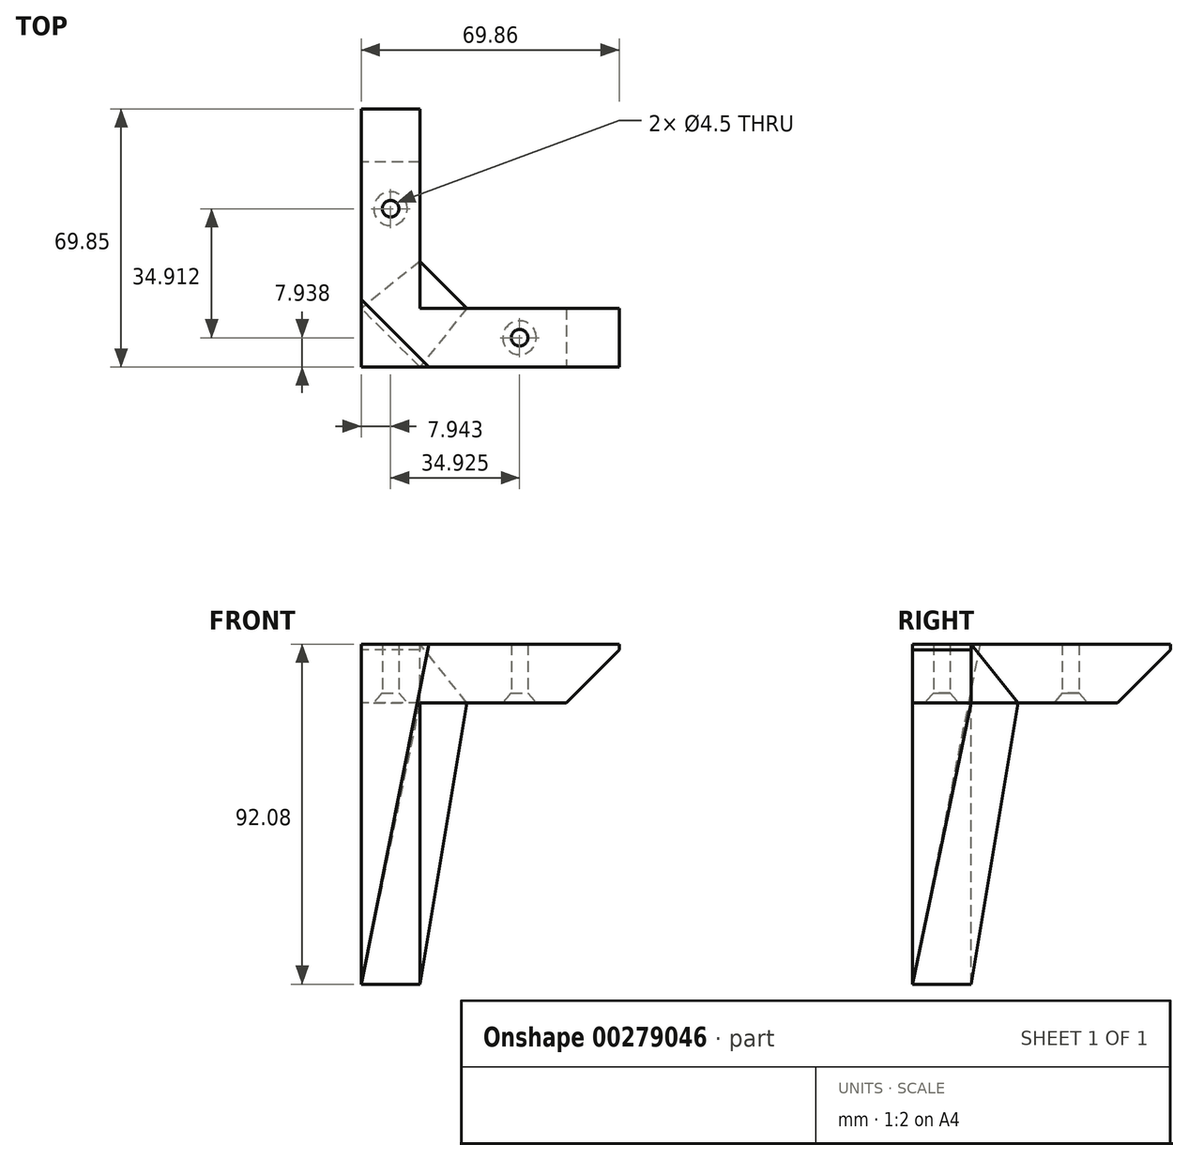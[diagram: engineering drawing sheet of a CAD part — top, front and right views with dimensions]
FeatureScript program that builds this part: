
annotation { "Feature Type Name" : "Feature", "Feature Type Description" : "" }
export const myFeature = defineFeature(function(context is Context, id is Id, definition is map)
    precondition{}
    {
        {
            var Q0;
            Q0=qCreatedBy(makeId("Top.planeOp"),FACE);
            var sketch = newSketch(context, id + "F0", { "sketchPlane" : qUnion([Q0])});
            skLineSegment(sketch, "E0.bottom", {"start": v(0, 0) * mm, "end": v(-15.88, 0) * mm});
            skLineSegment(sketch, "E0.top", {"start": v(0, 69.85) * mm, "end": v(-15.88, 69.85) * mm});
            skLineSegment(sketch, "E0.left", {"start": v(0, 15.87) * mm, "end": v(0, 69.85) * mm});
            skLineSegment(sketch, "E0.right", {"start": v(-15.88, 0) * mm, "end": v(-15.88, 69.85) * mm});
            skLineSegment(sketch, "E1.bottom", {"start": v(0, 0) * mm, "end": v(53.98, 0) * mm});
            skLineSegment(sketch, "E1.top", {"start": v(0, 15.87) * mm, "end": v(53.98, 15.87) * mm});
            skLineSegment(sketch, "E1.right", {"start": v(53.98, 0) * mm, "end": v(53.98, 15.87) * mm});
            skSolve(sketch);
        }
        {
            var Q0;
            Q0=makeQuery(id+"F0.imprint","IMPRINT",FACE,{"disambiguationData":[TD([[makeQuery(id+"F0.imprint","IMPRINT",EDGE,{"derivedFrom":sQuery(id+"F0.wireOp",EDGE,"E0.bottom")}),-1.0]])]});
            extrude(context, id + "F1", {"entities" : qUnion([Q0]), "depth" : 15.88 * mm});
        }
        {
            var Q0;
            Q0=makeQuery(id+"F1.opExtrude","CAP_FACE",FACE,{"disambiguationData":[OSD([sQuery(id+"F0.wireOp",EDGE,"E0.bottom"),sQuery(id+"F0.wireOp",EDGE,"E0.top"),sQuery(id+"F0.wireOp",EDGE,"E0.left"),sQuery(id+"F0.wireOp",EDGE,"E0.right"),sQuery(id+"F0.wireOp",EDGE,"E1.bottom"),sQuery(id+"F0.wireOp",EDGE,"E1.top"),sQuery(id+"F0.wireOp",EDGE,"E1.right")])],"isStart":true});
            var sketch = newSketch(context, id + "F2", { "sketchPlane" : qUnion([Q0])});
            skLineSegment(sketch, "E2.bottom", {"start": v(-15.88, 0) * mm, "end": v(0, 0) * mm});
            skLineSegment(sketch, "E2.top", {"start": v(-15.88, -15.87) * mm, "end": v(0, -15.87) * mm});
            skLineSegment(sketch, "E2.left", {"start": v(-15.88, 0) * mm, "end": v(-15.88, -15.87) * mm});
            skLineSegment(sketch, "E2.right", {"start": v(0, 0) * mm, "end": v(0, -15.87) * mm});
            skSolve(sketch);
        }
        {
            var Q0;
            Q0=makeQuery(id+"F2.imprint","IMPRINT",FACE,{"disambiguationData":[TD([[makeQuery(id+"F2.imprint","IMPRINT",EDGE,{"derivedFrom":sQuery(id+"F2.wireOp",EDGE,"E2.bottom")}),1.0]])]});
            extrude(context, id + "F3", {"entities" : qUnion([Q0]), "operationType" : NewBodyOperationType.ADD, "depth" : 76.2 * mm});
        }
        {
            var Q0;
            Q0=makeQuery(id+"F3.opExtrude","CAP_FACE",FACE,{"disambiguationData":[OSD([sQuery(id+"F2.wireOp",EDGE,"E2.bottom"),sQuery(id+"F2.wireOp",EDGE,"E2.top"),sQuery(id+"F2.wireOp",EDGE,"E2.left"),sQuery(id+"F2.wireOp",EDGE,"E2.right")])],"isStart":false});
            var sketch = newSketch(context, id + "F4", { "sketchPlane" : qUnion([Q0])});
            skLineSegment(sketch, "E3", {"start": v(-21.68, -5.8) * mm, "end": v(-5.62, 10.26) * mm});
            skSolve(sketch);
        }
        {
            var Q0;
            Q0=sQuery(id+"F4.wireOp",EDGE,"E3");
            cPlane(context, id + "F5", {"entities" : qUnion([Q0]), "cplaneType" : CPlaneType.LINE_ANGLE, "offset" : 25.4 * mm, "angle" : 82 * degree, "width" : 152.4 * mm, "height" : 152.4 * mm});
        }
        {
            var Q0;
            Q0=qCreatedBy(id+"F5.planeOp",FACE);
            var sketch = newSketch(context, id + "F6", { "sketchPlane" : qUnion([Q0])});
            skLineSegment(sketch, "E4.bottom", {"start": v(52.37, 33.7) * mm, "end": v(-53.54, 33.7) * mm});
            skLineSegment(sketch, "E4.top", {"start": v(52.37, -104.46) * mm, "end": v(-53.54, -104.46) * mm});
            skLineSegment(sketch, "E4.left", {"start": v(52.37, 33.7) * mm, "end": v(52.37, -104.46) * mm});
            skLineSegment(sketch, "E4.right", {"start": v(-53.54, 33.7) * mm, "end": v(-53.54, -104.46) * mm});
            skSolve(sketch);
        }
        {
            var Q0;
            Q0 = qSketchRegion(id + "F6", true);
            var Q1;
            Q1=makeQuery(id+"F1.opExtrude","CAP_VERTEX",VERTEX,{"disambiguationData":[OSD([sQuery(id+"F0.wireOp",EDGE,"E0.bottom"),sQuery(id+"F0.wireOp",EDGE,"E0.right")])],"isStart":false});
            extrude(context, id + "F7", {"entities" : qUnion([Q0]), "operationType" : NewBodyOperationType.REMOVE, "endBound" : BoundingType.UP_TO_VERTEX, "oppositeDirection" : true, "endBoundEntityVertex" : qUnion([Q1]), "depth" : 25.4 * mm});
        }
        {
            var Q0;
            Q0=makeQuery(id+"F4.imprint","IMPRINT",FACE,{"disambiguationData":[TD([[makeQuery(id+"F4.imprint","IMPRINT",EDGE,{"derivedFrom":makeQuery(id+"F3.opExtrude","CAP_EDGE",EDGE,{"disambiguationData":[OSD([sQuery(id+"F2.wireOp",EDGE,"E2.bottom")])],"isStart":false})}),1.0]])]});
            var sketch = newSketch(context, id + "F8", { "sketchPlane" : qUnion([Q0])});
            skLineSegment(sketch, "E5", {"start": v(8.34, -7.54) * mm, "end": v(-13.82, -29.7) * mm});
            skSolve(sketch);
        }
        {
            var Q0;
            {var subQ0=sQuery(id+"F0.wireOp",EDGE,"E0.right");var subQ1=sQuery(id+"F0.wireOp",EDGE,"E0.left");var subQ2=sQuery(id+"F0.wireOp",EDGE,"E0.top");var subQ3=sQuery(id+"F0.wireOp",EDGE,"E1.top");var subQ4=makeQuery(id+"F1.opExtrude","CAP_FACE",FACE,{"disambiguationData":[OSD([sQuery(id+"F0.wireOp",EDGE,"E0.bottom"),subQ2,subQ1,subQ0,sQuery(id+"F0.wireOp",EDGE,"E1.bottom"),subQ3,sQuery(id+"F0.wireOp",EDGE,"E1.right")])],"isStart":true});Q0=makeQuery(id+"F3.boolean.opBoolean","SPLIT",FACE,{"disambiguationData":[TD([makeQuery(id+"F1.opExtrude","SWEPT_FACE",FACE,{"disambiguationData":[OSD([subQ2])]})])],"derivedFrom":subQ4});}
            var sketch = newSketch(context, id + "F9", { "sketchPlane" : qUnion([Q0])});
            skLineSegment(sketch, "E6", {"start": v(0, -15.87) * mm, "end": v(0, -28.57) * mm});
            skLineSegment(sketch, "E7", {"start": v(0, -28.57) * mm, "end": v(-15.88, -15.87) * mm});
            skLineSegment(sketch, "E8", {"start": v(-15.88, -15.87) * mm, "end": v(0, -15.87) * mm});
            skSolve(sketch);
        }
        {
            var Q1;
            Q1=makeQuery(id+"F9.imprint","IMPRINT",FACE,{"disambiguationData":[TD([[makeQuery(id+"F9.imprint","IMPRINT",EDGE,{"derivedFrom":sQuery(id+"F9.wireOp",EDGE,"E6")}),-1.0]])]});
            var Q2;
            Q2=makeQuery(id+"F3.opExtrude","CAP_VERTEX",VERTEX,{"disambiguationData":[OSD([sQuery(id+"F0.wireOp",EDGE,"E0.right"),sQuery(id+"F2.wireOp",EDGE,"E2.top"),sQuery(id+"F2.wireOp",EDGE,"E2.left")])],"isStart":false});
            loft(context, id + "F10", {"operationType" : NewBodyOperationType.ADD, "sheetProfilesArray" : [{ "sheetProfileEntities" : qUnion([Q1]) }, { "sheetProfileEntities" : qUnion([Q2]) }]});
        }
        {
            var Q0;
            {var subQ0=sQuery(id+"F0.wireOp",EDGE,"E1.top");var subQ1=sQuery(id+"F0.wireOp",EDGE,"E0.left");var subQ2=sQuery(id+"F0.wireOp",EDGE,"E1.bottom");var subQ3=sQuery(id+"F0.wireOp",EDGE,"E0.bottom");var subQ4=sQuery(id+"F0.wireOp",EDGE,"E1.right");var subQ5=makeQuery(id+"F1.opExtrude","CAP_FACE",FACE,{"disambiguationData":[OSD([subQ3,sQuery(id+"F0.wireOp",EDGE,"E0.top"),subQ1,sQuery(id+"F0.wireOp",EDGE,"E0.right"),subQ2,subQ0,subQ4])],"isStart":true});Q0=makeQuery(id+"F3.boolean.opBoolean","SPLIT",FACE,{"disambiguationData":[TD([makeQuery(id+"F1.opExtrude","SWEPT_FACE",FACE,{"disambiguationData":[OSD([subQ4])]})])],"derivedFrom":subQ5});}
            var sketch = newSketch(context, id + "F11", { "sketchPlane" : qUnion([Q0])});
            skLineSegment(sketch, "E9", {"start": v(0, -15.87) * mm, "end": v(12.7, -15.87) * mm});
            skLineSegment(sketch, "E10", {"start": v(12.7, -15.87) * mm, "end": v(0, 0) * mm});
            skLineSegment(sketch, "E11", {"start": v(0, 0) * mm, "end": v(0, -15.87) * mm});
            skSolve(sketch);
        }
        {
            var Q1;
            Q1=makeQuery(id+"F11.imprint","IMPRINT",FACE,{"disambiguationData":[TD([[makeQuery(id+"F11.imprint","IMPRINT",EDGE,{"derivedFrom":sQuery(id+"F11.wireOp",EDGE,"E9")}),1.0]])]});
            var Q2;
            Q2=makeQuery(id+"F3.opExtrude","CAP_VERTEX",VERTEX,{"disambiguationData":[OSD([sQuery(id+"F0.wireOp",EDGE,"E0.bottom"),sQuery(id+"F0.wireOp",EDGE,"E1.bottom"),sQuery(id+"F2.wireOp",EDGE,"E2.bottom"),sQuery(id+"F2.wireOp",EDGE,"E2.right")])],"isStart":false});
            loft(context, id + "F12", {"operationType" : NewBodyOperationType.ADD, "sheetProfilesArray" : [{ "sheetProfileEntities" : qUnion([Q1]) }, { "sheetProfileEntities" : qUnion([Q2]) }]});
        }
        {
            var Q0;
            {var subQ0=sQuery(id+"F0.wireOp",EDGE,"E0.right");var subQ1=sQuery(id+"F0.wireOp",EDGE,"E0.left");var subQ2=sQuery(id+"F0.wireOp",EDGE,"E0.top");var subQ3=sQuery(id+"F0.wireOp",EDGE,"E1.top");var subQ4=makeQuery(id+"F1.opExtrude","CAP_FACE",FACE,{"disambiguationData":[OSD([sQuery(id+"F0.wireOp",EDGE,"E0.bottom"),subQ2,subQ1,subQ0,sQuery(id+"F0.wireOp",EDGE,"E1.bottom"),subQ3,sQuery(id+"F0.wireOp",EDGE,"E1.right")])],"isStart":true});Q0=makeQuery(id+"F3.boolean.opBoolean","SPLIT",FACE,{"disambiguationData":[TD([makeQuery(id+"F1.opExtrude","SWEPT_FACE",FACE,{"disambiguationData":[OSD([subQ2])]})])],"derivedFrom":subQ4});}
            var sketch = newSketch(context, id + "F13", { "sketchPlane" : qUnion([Q0])});
            skLineSegment(sketch, "E12", {"start": v(0, -15.87) * mm, "end": v(0, -28.57) * mm});
            skLineSegment(sketch, "E13", {"start": v(0, -15.87) * mm, "end": v(12.7, -15.87) * mm});
            skLineSegment(sketch, "E14", {"start": v(12.7, -15.87) * mm, "end": v(0, -28.57) * mm});
            skSolve(sketch);
        }
        {
            var Q1;
            Q1=makeQuery(id+"F13.imprint","IMPRINT",FACE,{"disambiguationData":[TD([[makeQuery(id+"F13.imprint","IMPRINT",EDGE,{"derivedFrom":sQuery(id+"F13.wireOp",EDGE,"E12")}),1.0]])]});
            var Q2;
            Q2=makeQuery(id+"F1.opExtrude","CAP_VERTEX",VERTEX,{"disambiguationData":[OSD([sQuery(id+"F0.wireOp",EDGE,"E0.left"),sQuery(id+"F0.wireOp",EDGE,"E1.top")])],"isStart":false});
            loft(context, id + "F14", {"operationType" : NewBodyOperationType.ADD, "sheetProfilesArray" : [{ "sheetProfileEntities" : qUnion([Q1]) }, { "sheetProfileEntities" : qUnion([Q2]) }]});
        }
        {
            var Q0;
            Q0=makeQuery(id+"F4.imprint","IMPRINT",FACE,{"disambiguationData":[TD([[makeQuery(id+"F4.imprint","IMPRINT",EDGE,{"derivedFrom":makeQuery(id+"F3.opExtrude","CAP_EDGE",EDGE,{"disambiguationData":[OSD([sQuery(id+"F2.wireOp",EDGE,"E2.bottom")])],"isStart":false})}),1.0]])]});
            var sketch = newSketch(context, id + "F15", { "sketchPlane" : qUnion([Q0])});
            skLineSegment(sketch, "E15", {"start": v(0, 0) * mm, "end": v(-15.88, -15.88) * mm});
            skLineSegment(sketch, "E16", {"start": v(0, 0) * mm, "end": v(0, -15.87) * mm});
            skLineSegment(sketch, "E17", {"start": v(-15.88, -15.88) * mm, "end": v(0, -15.88) * mm});
            skSolve(sketch);
        }
        {
            var Q1;
            Q1 = qSketchRegion(id + "F15", true);
            var Q2;
            {var subQ0=sQuery(id+"F0.wireOp",EDGE,"E1.top");var subQ1=sQuery(id+"F0.wireOp",EDGE,"E0.left");Q2=makeQuery(id+"F14.boolean.opBoolean","MERGE",VERTEX,{"derivedFrom":[makeQuery(id+"F12.boolean.opBoolean","MERGE",VERTEX,{"derivedFrom":[makeQuery(id+"F10.boolean.opBoolean","MERGE",VERTEX,{"derivedFrom":[makeQuery(id+"F3.boolean.opBoolean","MERGE",VERTEX,{"derivedFrom":[makeQuery(id+"F1.opExtrude","CAP_VERTEX",VERTEX,{"disambiguationData":[OSD([subQ1,subQ0])],"isStart":true}),makeQuery(id+"F3.opExtrude","CAP_VERTEX",VERTEX,{"disambiguationData":[OSD([subQ1,subQ0,sQuery(id+"F2.wireOp",EDGE,"E2.top"),sQuery(id+"F2.wireOp",EDGE,"E2.right")])],"isStart":true})]}),makeQuery(id+"F10.opLoft","MID_CAP_VERTEX",VERTEX,{"disambiguationData":[OSD([sQuery(id+"F9.wireOp",EDGE,"E6"),sQuery(id+"F9.wireOp",EDGE,"E8")])],"capPos":0.0})]}),makeQuery(id+"F12.opLoft","MID_CAP_VERTEX",VERTEX,{"disambiguationData":[OSD([sQuery(id+"F11.wireOp",EDGE,"E9"),sQuery(id+"F11.wireOp",EDGE,"E11")])],"capPos":0.0})]}),makeQuery(id+"F14.opLoft","MID_CAP_VERTEX",VERTEX,{"disambiguationData":[OSD([sQuery(id+"F13.wireOp",EDGE,"E12"),sQuery(id+"F13.wireOp",EDGE,"E13")])],"capPos":0.0})]});}
            loft(context, id + "F16", {"operationType" : NewBodyOperationType.REMOVE, "sheetProfilesArray" : [{ "sheetProfileEntities" : qUnion([Q1]) }, { "sheetProfileEntities" : qUnion([Q2]) }]});
        }
        {
            var Q0;
            Q0=makeQuery(id+"F10.opLoft","SWEPT_EDGE",EDGE,{"disambiguationData":[OSD([sQuery(id+"F0.wireOp",EDGE,"E0.left"),sQuery(id+"F0.wireOp",EDGE,"E0.right"),sQuery(id+"F2.wireOp",EDGE,"E2.top"),sQuery(id+"F2.wireOp",EDGE,"E2.left"),sQuery(id+"F9.wireOp",EDGE,"E6"),sQuery(id+"F9.wireOp",EDGE,"E7")])]});
            var Q1;
            Q1=makeQuery(id+"F12.opLoft","SWEPT_EDGE",EDGE,{"disambiguationData":[OSD([sQuery(id+"F0.wireOp",EDGE,"E0.bottom"),sQuery(id+"F0.wireOp",EDGE,"E1.bottom"),sQuery(id+"F0.wireOp",EDGE,"E1.top"),sQuery(id+"F2.wireOp",EDGE,"E2.bottom"),sQuery(id+"F2.wireOp",EDGE,"E2.right"),sQuery(id+"F11.wireOp",EDGE,"E9"),sQuery(id+"F11.wireOp",EDGE,"E10")])]});
            cPlane(context, id + "F17", {"entities" : qUnion([Q0, Q1]), "cplaneType" : CPlaneType.LINE_ANGLE, "offset" : 25.4 * mm, "angle" : 0 * degree, "width" : 152.4 * mm, "height" : 152.4 * mm});
        }
        {
            var Q1;
            Q1=makeQuery(id+"F14.opLoft","CAP_FACE",FACE,{"disambiguationData":[OSD([makeQuery(id+"F13.imprint","IMPRINT",FACE,{"disambiguationData":[TD([[makeQuery(id+"F13.imprint","IMPRINT",EDGE,{"derivedFrom":sQuery(id+"F13.wireOp",EDGE,"E12")}),1.0]])]})])],"isStart":true});
            var Q2;
            Q2=makeQuery(id+"F3.opExtrude","CAP_FACE",FACE,{"disambiguationData":[OSD([sQuery(id+"F2.wireOp",EDGE,"E2.bottom"),sQuery(id+"F2.wireOp",EDGE,"E2.top"),sQuery(id+"F2.wireOp",EDGE,"E2.left"),sQuery(id+"F2.wireOp",EDGE,"E2.right")])],"isStart":false});
            loft(context, id + "F18", {"operationType" : NewBodyOperationType.ADD, "sheetProfilesArray" : [{ "sheetProfileEntities" : qUnion([Q1]) }, { "sheetProfileEntities" : qUnion([Q2]) }]});
        }
        {
            var Q0;
            Q0=makeQuery(id+"F3.boolean.opBoolean","MERGE",FACE,{"derivedFrom":[makeQuery(id+"F1.opExtrude","SWEPT_FACE",FACE,{"disambiguationData":[OSD([sQuery(id+"F0.wireOp",EDGE,"E0.right")])]}),makeQuery(id+"F3.opExtrude","SWEPT_FACE",FACE,{"disambiguationData":[OSD([sQuery(id+"F2.wireOp",EDGE,"E2.left")])]})]});
            var sketch = newSketch(context, id + "F19", { "sketchPlane" : qUnion([Q0])});
            skLineSegment(sketch, "E18", {"start": v(-69.85, 0) * mm, "end": v(-69.85, 14.29) * mm});
            skLineSegment(sketch, "E19", {"start": v(-69.85, 14.29) * mm, "end": v(-55.55, 0) * mm});
            skLineSegment(sketch, "E20", {"start": v(-69.85, 0) * mm, "end": v(-55.55, 0) * mm});
            skSolve(sketch);
        }
        {
            var Q0;
            Q0=makeQuery(id+"F19.imprint","IMPRINT",FACE,{"disambiguationData":[TD([[makeQuery(id+"F19.imprint","IMPRINT",EDGE,{"derivedFrom":sQuery(id+"F19.wireOp",EDGE,"E18")}),1.0]])]});
            extrude(context, id + "F20", {"entities" : qUnion([Q0]), "operationType" : NewBodyOperationType.REMOVE, "endBound" : BoundingType.UP_TO_NEXT, "oppositeDirection" : true, "depth" : 25.4 * mm});
        }
        {
            var Q0;
            Q0=makeQuery(id+"F3.boolean.opBoolean","MERGE",FACE,{"derivedFrom":[makeQuery(id+"F1.opExtrude","SWEPT_FACE",FACE,{"disambiguationData":[OSD([sQuery(id+"F0.wireOp",EDGE,"E0.bottom"),sQuery(id+"F0.wireOp",EDGE,"E1.bottom")])]}),makeQuery(id+"F3.opExtrude","SWEPT_FACE",FACE,{"disambiguationData":[OSD([sQuery(id+"F2.wireOp",EDGE,"E2.bottom")])]})]});
            var sketch = newSketch(context, id + "F21", { "sketchPlane" : qUnion([Q0])});
            skLineSegment(sketch, "E21", {"start": v(53.98, 0) * mm, "end": v(53.98, 14.29) * mm});
            skLineSegment(sketch, "E22", {"start": v(53.98, 0) * mm, "end": v(39.69, 0) * mm});
            skLineSegment(sketch, "E23", {"start": v(39.69, 0) * mm, "end": v(53.98, 14.29) * mm});
            skSolve(sketch);
        }
        {
            var Q0;
            Q0=makeQuery(id+"F21.imprint","IMPRINT",FACE,{"disambiguationData":[TD([[makeQuery(id+"F21.imprint","IMPRINT",EDGE,{"derivedFrom":sQuery(id+"F21.wireOp",EDGE,"E21")}),-1.0]])]});
            extrude(context, id + "F22", {"entities" : qUnion([Q0]), "operationType" : NewBodyOperationType.REMOVE, "endBound" : BoundingType.UP_TO_NEXT, "oppositeDirection" : true, "depth" : 25.4 * mm});
        }
        {
            var Q0;
            {var subQ0=sQuery(id+"F0.wireOp",EDGE,"E0.right");var subQ1=sQuery(id+"F0.wireOp",EDGE,"E0.left");var subQ2=sQuery(id+"F0.wireOp",EDGE,"E0.top");var subQ3=sQuery(id+"F0.wireOp",EDGE,"E1.top");var subQ4=makeQuery(id+"F1.opExtrude","CAP_FACE",FACE,{"disambiguationData":[OSD([sQuery(id+"F0.wireOp",EDGE,"E0.bottom"),subQ2,subQ1,subQ0,sQuery(id+"F0.wireOp",EDGE,"E1.bottom"),subQ3,sQuery(id+"F0.wireOp",EDGE,"E1.right")])],"isStart":true});Q0=makeQuery(id+"F3.boolean.opBoolean","SPLIT",FACE,{"disambiguationData":[TD([makeQuery(id+"F1.opExtrude","SWEPT_FACE",FACE,{"disambiguationData":[OSD([subQ2])]})])],"derivedFrom":subQ4});}
            var sketch = newSketch(context, id + "F23", { "sketchPlane" : qUnion([Q0])});
            skLineSegment(sketch, "E24", {"start": v(-15.88, -42.85) * mm, "end": v(0, -42.85) * mm, "construction": true});
            skCircle(sketch, "E25", {"center": v(-7.94, -42.85) * mm, "radius": 4.14 * mm, "construction": true});
            skLineSegment(sketch, "E26", {"start": v(26.99, -15.87) * mm, "end": v(26.99, 0) * mm, "construction": true});
            skCircle(sketch, "E27", {"center": v(26.99, -7.94) * mm, "radius": 3.1 * mm, "construction": true});
            skSolve(sketch);
        }
        {
            var Q0;
            Q0=sQuery(id+"F23.wireOp",VERTEX,"E25.center");
            var Q1;
            Q1=sQuery(id+"F23.wireOp",VERTEX,"E27.center");
            var Q2;
            Q2=makeQuery(id+"F1.opExtrude","SWEPT_BODY",BODY,{"disambiguationData":[OSD([sQuery(id+"F0.wireOp",EDGE,"E0.bottom"),sQuery(id+"F0.wireOp",EDGE,"E0.top"),sQuery(id+"F0.wireOp",EDGE,"E0.left"),sQuery(id+"F0.wireOp",EDGE,"E0.right"),sQuery(id+"F0.wireOp",EDGE,"E1.bottom"),sQuery(id+"F0.wireOp",EDGE,"E1.top"),sQuery(id+"F0.wireOp",EDGE,"E1.right")])]});
            hole(context, id + "F24", {"style" : HoleStyle.C_SINK, "endStyle" : HoleEndStyle.BLIND, "standardTappedOrClearance" : lookupTablePath({ "standard" : "ANSI", "fit" : "Normal (ASME)", "size" : "#8", "type" : "Clearance" }), "standardBlindInLast" : lookupTablePath({ "fit" : "Free", "standard" : "ANSI", "size" : "#8", "type" : "Clearance" }), "holeDiameter" : 4.5 * mm, "cSinkDiameter" : 9.12 * mm, "cSinkAngle" : 82 * degree, "holeDepth" : 15.88 * mm, "tappedDepth" : 12.7 * mm, "tapClearance" : 3, "locations" : qUnion([Q0, Q1]), "scope" : qUnion([Q2])});
        }
    });
